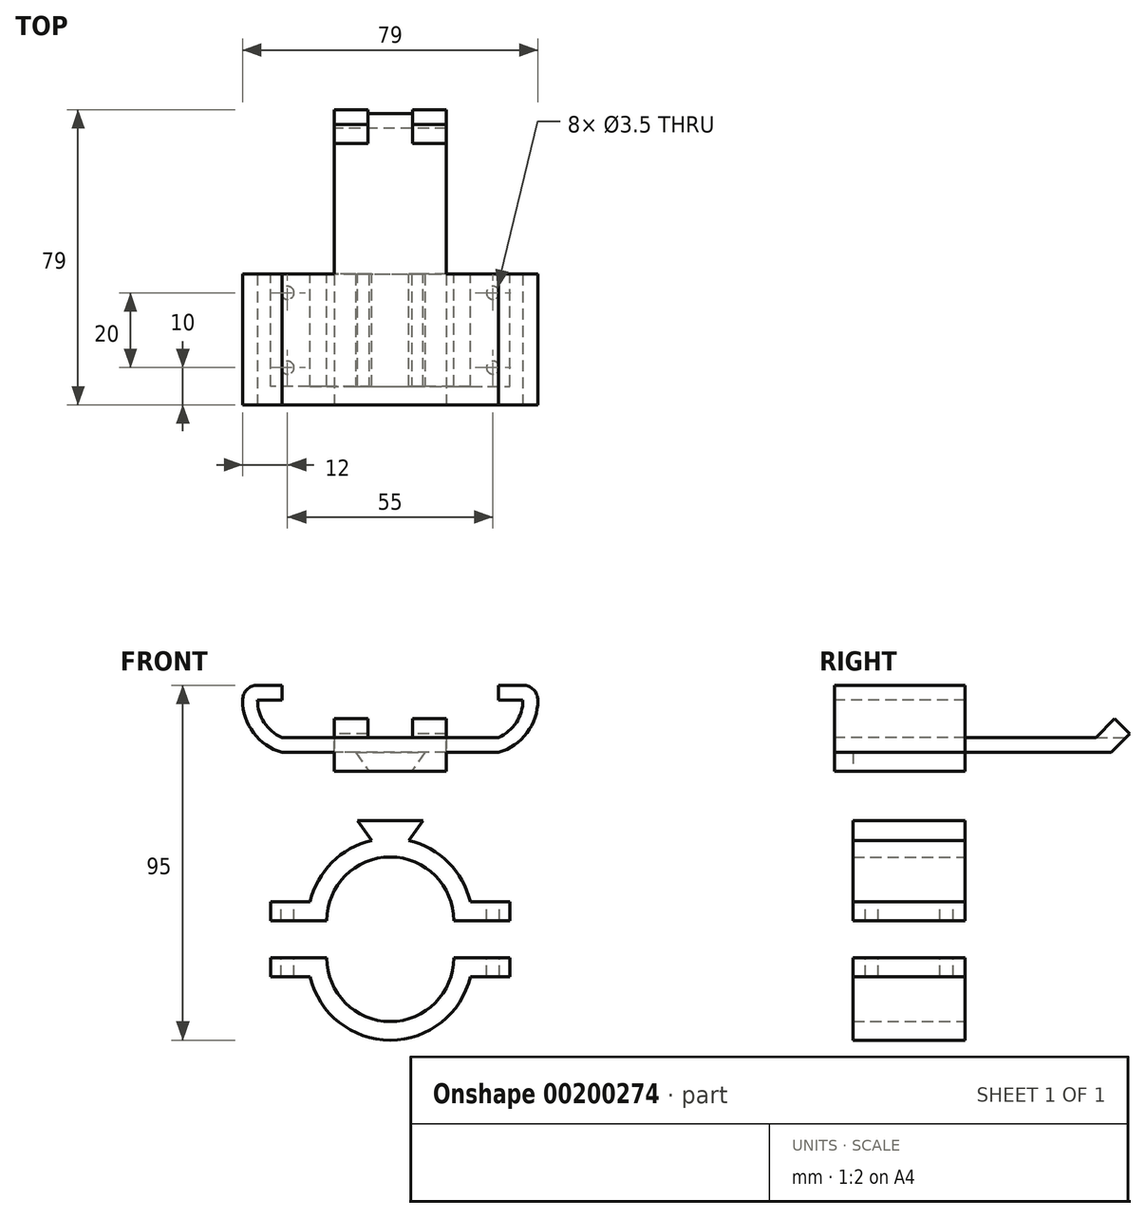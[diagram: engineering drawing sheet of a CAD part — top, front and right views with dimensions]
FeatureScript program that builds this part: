
annotation { "Feature Type Name" : "Feature", "Feature Type Description" : "" }
export const myFeature = defineFeature(function(context is Context, id is Id, definition is map)
    precondition{}
    {
        {
            var Q0;
            Q0=qCreatedBy(makeId("Front.planeOp"),FACE);
            var sketch = newSketch(context, id + "F0", { "sketchPlane" : qUnion([Q0])});
            skArc(sketch, "E0", {"start": v(17, 0) * mm, "mid": v(0, 17) * mm, "end": v(-17, 0) * mm});
            skArc(sketch, "E1", {"start": v(22, 0) * mm, "mid": v(0, 22) * mm, "end": v(-22, 0) * mm});
            skLineSegment(sketch, "E2", {"start": v(17, 0) * mm, "end": v(-17, 0) * mm, "construction": true});
            skLineSegment(sketch, "E3", {"start": v(22, 0) * mm, "end": v(17, 0) * mm});
            skLineSegment(sketch, "E4", {"start": v(-17, 0) * mm, "end": v(-22, 0) * mm});
            skLineSegment(sketch, "E5.bottom", {"start": v(17, 0) * mm, "end": v(32, 0) * mm});
            skLineSegment(sketch, "E5.top", {"start": v(17, 5) * mm, "end": v(32, 5) * mm});
            skLineSegment(sketch, "E5.left", {"start": v(17, 0) * mm, "end": v(17, 5) * mm});
            skLineSegment(sketch, "E5.right", {"start": v(32, 0) * mm, "end": v(32, 5) * mm});
            skLineSegment(sketch, "E6.bottom", {"start": v(-17, 0) * mm, "end": v(-32, 0) * mm});
            skLineSegment(sketch, "E6.top", {"start": v(-17, 5) * mm, "end": v(-32, 5) * mm});
            skLineSegment(sketch, "E6.left", {"start": v(-17, 0) * mm, "end": v(-17, 5) * mm});
            skLineSegment(sketch, "E6.right", {"start": v(-32, 0) * mm, "end": v(-32, 5) * mm});
            skLineSegment(sketch, "E7", {"start": v(-17, -10) * mm, "end": v(17, -10) * mm, "construction": true});
            skArc(sketch, "E8", {"start": v(-17, -10) * mm, "mid": v(0, -27) * mm, "end": v(17, -10) * mm});
            skLineSegment(sketch, "E9", {"start": v(17, -10) * mm, "end": v(22, -10) * mm});
            skLineSegment(sketch, "E10", {"start": v(-17, -10) * mm, "end": v(-22, -10) * mm});
            skArc(sketch, "E11", {"start": v(-22, -10) * mm, "mid": v(0, -32) * mm, "end": v(22, -10) * mm});
            skLineSegment(sketch, "E12.bottom", {"start": v(17, -10) * mm, "end": v(32, -10) * mm});
            skLineSegment(sketch, "E12.top", {"start": v(17, -15) * mm, "end": v(32, -15) * mm});
            skLineSegment(sketch, "E12.left", {"start": v(17, -10) * mm, "end": v(17, -15) * mm});
            skLineSegment(sketch, "E12.right", {"start": v(32, -10) * mm, "end": v(32, -15) * mm});
            skPoint(sketch, "E13.oppositeSnap0", {"position": v(24.5, -15) * mm});
            skLineSegment(sketch, "E13.bottom", {"start": v(-17, -10) * mm, "end": v(-32, -10) * mm});
            skLineSegment(sketch, "E13.top", {"start": v(-17, -15) * mm, "end": v(-32, -15) * mm});
            skLineSegment(sketch, "E13.left", {"start": v(-17, -10) * mm, "end": v(-17, -15) * mm});
            skLineSegment(sketch, "E13.right", {"start": v(-32, -10) * mm, "end": v(-32, -15) * mm});
            skPoint(sketch, "E14", {"position": v(0, 21.42) * mm});
            skLineSegment(sketch, "E15", {"start": v(-5, 21.42) * mm, "end": v(5, 21.42) * mm, "construction": true});
            skLineSegment(sketch, "E16", {"start": v(-5, 21.42) * mm, "end": v(-8.75, 26.78) * mm});
            skLineSegment(sketch, "E17", {"start": v(-8.75, 26.78) * mm, "end": v(8.75, 26.78) * mm});
            skLineSegment(sketch, "E18", {"start": v(8.75, 26.78) * mm, "end": v(5, 21.42) * mm});
            skPoint(sketch, "E19.endSnap0", {"position": v(0, 17) * mm});
            skSolve(sketch);
        }
        {
            var Q0;
            Q0=qCreatedBy(makeId("Front.planeOp"),FACE);
            cPlane(context, id + "F1", {"entities" : qUnion([Q0]), "cplaneType" : CPlaneType.OFFSET, "offset" : 30 * mm, "width" : 150 * mm, "height" : 150 * mm});
        }
        {
            var Q0;
            Q0=qCreatedBy(id+"F1.planeOp",FACE);
            var sketch = newSketch(context, id + "F2", { "sketchPlane" : qUnion([Q0])});
            skLineSegment(sketch, "E20", {"start": v(-29, 49) * mm, "end": v(29, 49) * mm});
            skLineSegment(sketch, "E21", {"start": v(-35.5, 59) * mm, "end": v(35.5, 59) * mm, "construction": true});
            skLineSegment(sketch, "E22", {"start": v(0, 49) * mm, "end": v(0, 59) * mm, "construction": true});
            skArc(sketch, "E23", {"start": v(29, 49) * mm, "mid": v(33.73, 53.04) * mm, "end": v(35.5, 59) * mm});
            skArc(sketch, "E24", {"start": v(-35.5, 59) * mm, "mid": v(-33.73, 53.04) * mm, "end": v(-29, 49) * mm});
            skLineSegment(sketch, "E25", {"start": v(-9.25, 45) * mm, "end": v(9.25, 45) * mm});
            skLineSegment(sketch, "E26", {"start": v(9.25, 45) * mm, "end": v(5.75, 40) * mm});
            skLineSegment(sketch, "E27", {"start": v(-9.25, 45) * mm, "end": v(-5.75, 40) * mm});
            skLineSegment(sketch, "E28", {"start": v(35.5, 59) * mm, "end": v(29, 59) * mm});
            skLineSegment(sketch, "E29", {"start": v(29, 59) * mm, "end": v(29, 63) * mm});
            skLineSegment(sketch, "E30", {"start": v(29, 63) * mm, "end": v(35.5, 63) * mm});
            skLineSegment(sketch, "E31", {"start": v(5.75, 40) * mm, "end": v(15, 40) * mm});
            skLineSegment(sketch, "E32", {"start": v(15, 40) * mm, "end": v(15, 45) * mm});
            skLineSegment(sketch, "E33", {"start": v(15, 45) * mm, "end": v(29, 45) * mm});
            skArc(sketch, "E34", {"start": v(29, 45) * mm, "mid": v(36.58, 50.25) * mm, "end": v(39.5, 59) * mm});
            skLineSegment(sketch, "E35", {"start": v(-5.75, 40) * mm, "end": v(-15, 40) * mm});
            skLineSegment(sketch, "E36", {"start": v(-15, 40) * mm, "end": v(-15, 45) * mm});
            skLineSegment(sketch, "E37", {"start": v(-15, 45) * mm, "end": v(-29, 45) * mm});
            skLineSegment(sketch, "E38", {"start": v(-35.5, 59) * mm, "end": v(-29, 59) * mm});
            skLineSegment(sketch, "E39", {"start": v(-29, 59) * mm, "end": v(-29, 63) * mm});
            skLineSegment(sketch, "E40", {"start": v(-29, 63) * mm, "end": v(-35.5, 63) * mm});
            skArc(sketch, "E41", {"start": v(-39.5, 59) * mm, "mid": v(-36.58, 50.25) * mm, "end": v(-29, 45) * mm});
            skArc(sketch, "E42", {"start": v(39.5, 59) * mm, "mid": v(38.33, 61.83) * mm, "end": v(35.5, 63) * mm});
            skArc(sketch, "E43", {"start": v(-35.5, 63) * mm, "mid": v(-38.33, 61.83) * mm, "end": v(-39.5, 59) * mm});
            skPoint(sketch, "E44", {"position": v(0, 45) * mm});
            skLineSegment(sketch, "E45", {"start": v(-5.75, 40) * mm, "end": v(5.75, 40) * mm});
            skLineSegment(sketch, "E46", {"start": v(0, 40) * mm, "end": v(0, 0) * mm, "construction": true});
            skSolve(sketch);
        }
        {
            var Q0;
            Q0=makeQuery(id+"F0.imprint","IMPRINT",FACE,{"disambiguationData":[TD([[makeQuery(id+"F0.imprint","IMPRINT",EDGE,{"derivedFrom":sQuery(id+"F0.wireOp",EDGE,"mbzJrH7V-MKxJ-bzjF-v4ra-i13s79XAPloW")}),-1.0]])]});
            var Q1;
            Q1=makeQuery(id+"F2.imprint","IMPRINT",FACE,{"disambiguationData":[TD([[makeQuery(id+"F2.imprint","IMPRINT",EDGE,{"derivedFrom":sQuery(id+"F2.wireOp",EDGE,"E20")}),-1.0]])]});
            extrude(context, id + "F3", {"entities" : qUnion([Q0, Q1]), "oppositeDirection" : true, "depth" : 30 * mm});
        }
        {
            var Q0;
            Q0=makeQuery(id+"F2.imprint","IMPRINT",FACE,{"disambiguationData":[TD([[makeQuery(id+"F2.imprint","IMPRINT",EDGE,{"derivedFrom":sQuery(id+"F2.wireOp",EDGE,"E20")}),-1.0]])]});
            var Q1;
            Q1=makeQuery(id+"F2.imprint","IMPRINT",FACE,{"disambiguationData":[TD([[makeQuery(id+"F2.imprint","IMPRINT",EDGE,{"derivedFrom":sQuery(id+"F2.wireOp",EDGE,"E25")}),-1.0]])]});
            extrude(context, id + "F4", {"entities" : qUnion([Q0, Q1]), "operationType" : NewBodyOperationType.ADD, "depth" : 5 * mm});
        }
        {
            var Q0;
            Q0=qCreatedBy(makeId("Right.planeOp"),FACE);
            var sketch = newSketch(context, id + "F5", { "sketchPlane" : qUnion([Q0])});
            skLineSegment(sketch, "E47.left", {"start": v(0, 49) * mm, "end": v(0, 45) * mm});
            skLineSegment(sketch, "E48", {"start": v(0, 49) * mm, "end": v(35, 49) * mm});
            skPoint(sketch, "E49", {"position": v(0, 59) * mm});
            skPoint(sketch, "E50", {"position": v(0, 63) * mm});
            skLineSegment(sketch, "E51", {"start": v(35, 49) * mm, "end": v(40, 54) * mm});
            skLineSegment(sketch, "E52", {"start": v(35, 49) * mm, "end": v(39, 45) * mm, "construction": true});
            skLineSegment(sketch, "E53", {"start": v(0, 45) * mm, "end": v(39, 45) * mm});
            skLineSegment(sketch, "E54", {"start": v(39, 45) * mm, "end": v(44, 50) * mm});
            skLineSegment(sketch, "E55", {"start": v(44, 50) * mm, "end": v(40, 54) * mm});
            skLineSegment(sketch, "E56", {"start": v(35, 49) * mm, "end": v(43, 49) * mm});
            skSolve(sketch);
        }
        {
            var Q0;
            Q0 = qSketchRegion(id + "F5", true);
            extrude(context, id + "F6", {"entities" : qUnion([Q0]), "operationType" : NewBodyOperationType.ADD, "depth" : 15 * mm, "hasSecondDirection" : true, "secondDirectionOppositeDirection" : true, "secondDirectionDepth" : 15 * mm});
        }
        {
            var Q0;
            Q0=makeQuery(id+"F5.imprint","IMPRINT",FACE,{"disambiguationData":[TD([[makeQuery(id+"F5.imprint","IMPRINT",EDGE,{"derivedFrom":sQuery(id+"F5.wireOp",EDGE,"E51")}),-1.0]])]});
            extrude(context, id + "F7", {"entities" : qUnion([Q0]), "operationType" : NewBodyOperationType.REMOVE, "endBound" : BoundingType.SYMMETRIC, "oppositeDirection" : true, "depth" : 12 * mm, "hasSecondDirection" : true, "secondDirectionOppositeDirection" : true, "secondDirectionDepth" : 6 * mm});
        }
        {
            var Q0;
            {var subQ5=sQuery(id+"F0.wireOp",EDGE,"E6.right");Q0=makeQuery(id+"F0.imprint","IMPRINT",FACE,{"disambiguationData":[TD([[makeQuery(id+"F0.imprint","IMPRINT",EDGE,{"derivedFrom":subQ5}),-1.0]])]});}
            var Q1;
            {var subQ5=sQuery(id+"F0.wireOp",EDGE,"E6.left");Q1=makeQuery(id+"F0.imprint","IMPRINT",FACE,{"disambiguationData":[TD([[makeQuery(id+"F0.imprint","IMPRINT",EDGE,{"derivedFrom":subQ5}),1.0]])]});}
            var Q2;
            Q2=makeQuery(id+"F0.imprint","IMPRINT",FACE,{"disambiguationData":[TD([[makeQuery(id+"F0.imprint","IMPRINT",EDGE,{"derivedFrom":sQuery(id+"F0.wireOp",EDGE,"E0")}),-1.0]])]});
            var Q3;
            {var subQ5=sQuery(id+"F0.wireOp",EDGE,"E5.left");Q3=makeQuery(id+"F0.imprint","IMPRINT",FACE,{"disambiguationData":[TD([[makeQuery(id+"F0.imprint","IMPRINT",EDGE,{"derivedFrom":subQ5}),-1.0]])]});}
            var Q4;
            {var subQ5=sQuery(id+"F0.wireOp",EDGE,"E5.right");Q4=makeQuery(id+"F0.imprint","IMPRINT",FACE,{"disambiguationData":[TD([[makeQuery(id+"F0.imprint","IMPRINT",EDGE,{"derivedFrom":subQ5}),1.0]])]});}
            var Q5;
            {var subQ0=sQuery(id+"F0.wireOp",EDGE,"E16");Q5=makeQuery(id+"F0.imprint","IMPRINT",FACE,{"disambiguationData":[TD([[makeQuery(id+"F0.imprint","IMPRINT",EDGE,{"derivedFrom":subQ0}),-1.0]])]});}
            extrude(context, id + "F8", {"entities" : qUnion([Q0, Q1, Q2, Q3, Q4, Q5]), "depth" : 30 * mm});
        }
        {
            var Q0;
            {var subQ5=sQuery(id+"F0.wireOp",EDGE,"E13.right");Q0=makeQuery(id+"F0.imprint","IMPRINT",FACE,{"disambiguationData":[TD([[makeQuery(id+"F0.imprint","IMPRINT",EDGE,{"derivedFrom":subQ5}),1.0]])]});}
            var Q1;
            {var subQ5=sQuery(id+"F0.wireOp",EDGE,"E13.left");Q1=makeQuery(id+"F0.imprint","IMPRINT",FACE,{"disambiguationData":[TD([[makeQuery(id+"F0.imprint","IMPRINT",EDGE,{"derivedFrom":subQ5}),-1.0]])]});}
            var Q2;
            Q2=makeQuery(id+"F0.imprint","IMPRINT",FACE,{"disambiguationData":[TD([[makeQuery(id+"F0.imprint","IMPRINT",EDGE,{"derivedFrom":sQuery(id+"F0.wireOp",EDGE,"E8")}),-1.0]])]});
            var Q3;
            {var subQ5=sQuery(id+"F0.wireOp",EDGE,"E12.left");Q3=makeQuery(id+"F0.imprint","IMPRINT",FACE,{"disambiguationData":[TD([[makeQuery(id+"F0.imprint","IMPRINT",EDGE,{"derivedFrom":subQ5}),1.0]])]});}
            var Q4;
            {var subQ5=sQuery(id+"F0.wireOp",EDGE,"E12.right");Q4=makeQuery(id+"F0.imprint","IMPRINT",FACE,{"disambiguationData":[TD([[makeQuery(id+"F0.imprint","IMPRINT",EDGE,{"derivedFrom":subQ5}),-1.0]])]});}
            extrude(context, id + "F9", {"entities" : qUnion([Q0, Q1, Q2, Q3, Q4]), "depth" : 30 * mm});
        }
        {
            var Q0;
            Q0=makeQuery(id+"F8.opExtrude","SWEPT_FACE",FACE,{"disambiguationData":[OSD([sQuery(id+"F0.wireOp",EDGE,"E6.top")])]});
            var sketch = newSketch(context, id + "F10", { "sketchPlane" : qUnion([Q0])});
            skCircle(sketch, "E57", {"center": v(-27.5, -25) * mm, "radius": 1.75 * mm});
            skCircle(sketch, "E58", {"center": v(-27.5, -5) * mm, "radius": 1.75 * mm});
            skCircle(sketch, "E59", {"center": v(27.5, -5) * mm, "radius": 1.75 * mm});
            skCircle(sketch, "E60", {"center": v(27.5, -25) * mm, "radius": 1.75 * mm});
            skLineSegment(sketch, "E61", {"start": v(27.5, -15) * mm, "end": v(-27.5, -15) * mm, "construction": true});
            skLineSegment(sketch, "E62", {"start": v(-27.5, -5) * mm, "end": v(-27.5, -25) * mm, "construction": true});
            skLineSegment(sketch, "E63", {"start": v(27.5, -5) * mm, "end": v(27.5, -25) * mm, "construction": true});
            skLineSegment(sketch, "E64", {"start": v(0, 0) * mm, "end": v(0, -15) * mm, "construction": true});
            skSolve(sketch);
        }
        {
            var Q0;
            Q0 = qSketchRegion(id + "F10", true);
            extrude(context, id + "F11", {"entities" : qUnion([Q0]), "operationType" : NewBodyOperationType.REMOVE, "oppositeDirection" : true, "depth" : 50 * mm});
        }
    });
